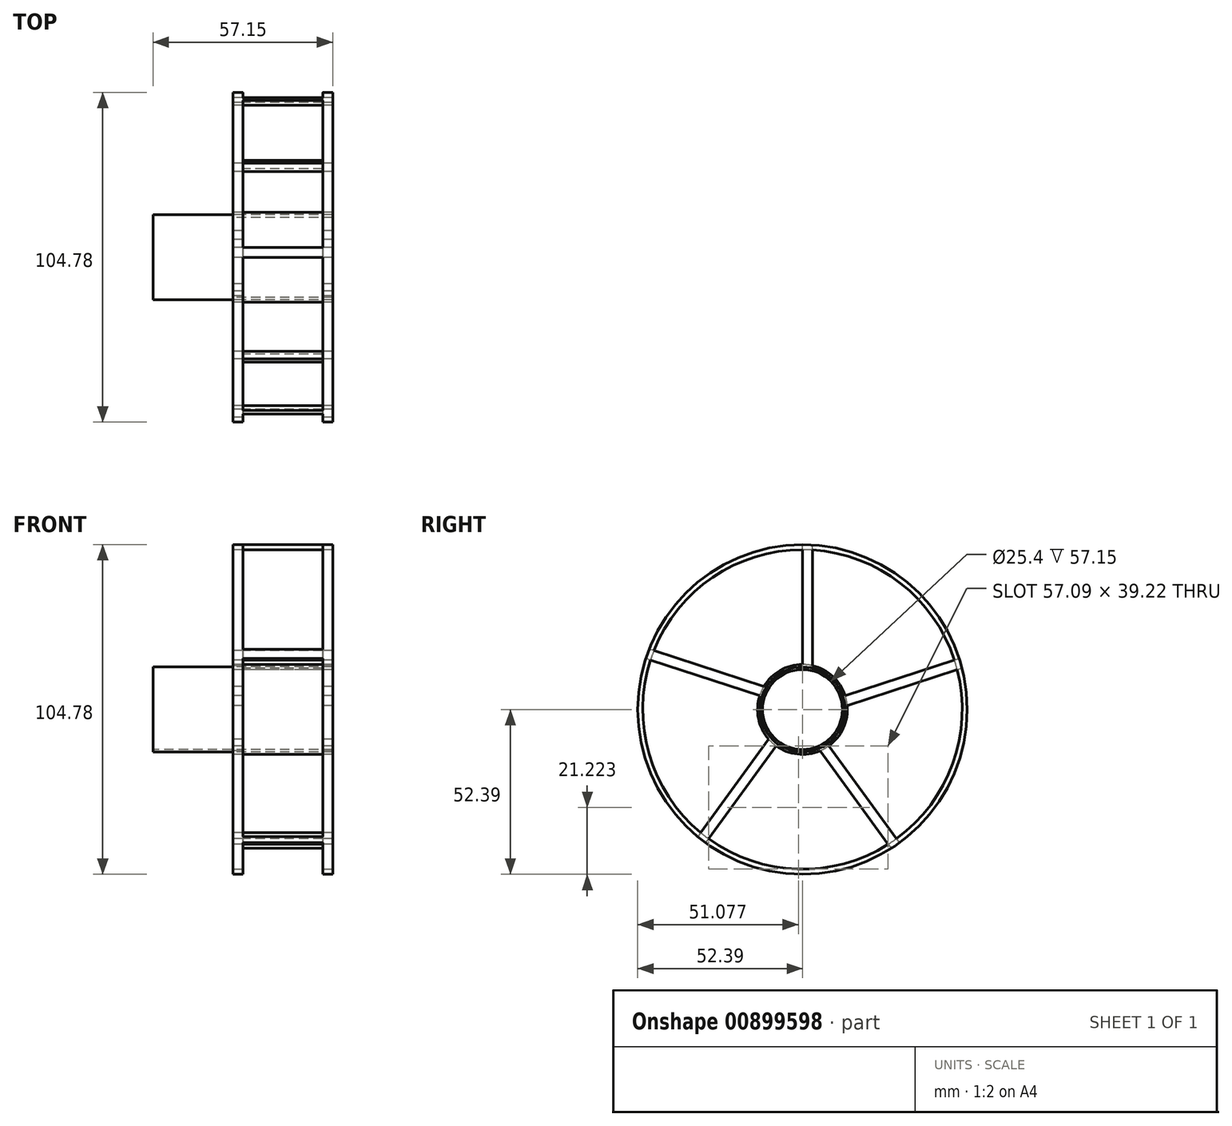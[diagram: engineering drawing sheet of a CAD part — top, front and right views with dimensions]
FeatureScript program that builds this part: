
annotation { "Feature Type Name" : "Feature", "Feature Type Description" : "" }
export const myFeature = defineFeature(function(context is Context, id is Id, definition is map)
    precondition{}
    {
        {
            var Q0;
            Q0=qCreatedBy(makeId("Right.planeOp"),FACE);
            var sketch = newSketch(context, id + "F0", { "sketchPlane" : qUnion([Q0])});
            skCircle(sketch, "E0", {"center": v(0, 0) * mm, "radius": 50.8 * mm});
            skCircle(sketch, "E1", {"center": v(0, 0) * mm, "radius": 52.39 * mm});
            skCircle(sketch, "E2", {"center": v(0, 0) * mm, "radius": 13.5 * mm});
            skCircle(sketch, "E3", {"center": v(0, 0) * mm, "radius": 12.7 * mm});
            skCircle(sketch, "E4", {"center": v(0, 0) * mm, "radius": 14.29 * mm});
            skLineSegment(sketch, "E5", {"start": v(0, 52.39) * mm, "end": v(0, 50.8) * mm});
            skLineSegment(sketch, "E6.0", {"start": v(3.17, 52.3) * mm, "end": v(3.17, 50.7) * mm});
            skLineSegment(sketch, "E7.1.0", {"start": v(-49.82, 16.19) * mm, "end": v(-48.31, 15.7) * mm});
            skLineSegment(sketch, "E7.1.1", {"start": v(-48.75, 19.18) * mm, "end": v(-47.24, 18.69) * mm});
            skLineSegment(sketch, "E7.2.0", {"start": v(-30.8, -42.38) * mm, "end": v(-29.86, -41.1) * mm});
            skLineSegment(sketch, "E7.2.1", {"start": v(-33.3, -40.44) * mm, "end": v(-32.37, -39.15) * mm});
            skLineSegment(sketch, "E7.3.0", {"start": v(30.8, -42.38) * mm, "end": v(29.86, -41.1) * mm});
            skLineSegment(sketch, "E7.3.1", {"start": v(28.17, -44.17) * mm, "end": v(27.23, -42.88) * mm});
            skLineSegment(sketch, "E7.4.0", {"start": v(49.82, 16.19) * mm, "end": v(48.31, 15.7) * mm});
            skLineSegment(sketch, "E7.4.1", {"start": v(50.71, 13.14) * mm, "end": v(49.2, 12.65) * mm});
            skLineSegment(sketch, "E8", {"start": v(0, 50.8) * mm, "end": v(0, 14.29) * mm});
            skLineSegment(sketch, "E9", {"start": v(3.17, 50.7) * mm, "end": v(3.17, 13.93) * mm});
            skLineSegment(sketch, "E10.1.0", {"start": v(-47.24, 18.69) * mm, "end": v(-12.27, 7.32) * mm});
            skLineSegment(sketch, "E10.1.1", {"start": v(-48.31, 15.7) * mm, "end": v(-13.59, 4.42) * mm});
            skLineSegment(sketch, "E10.2.0", {"start": v(-32.37, -39.15) * mm, "end": v(-10.76, -9.4) * mm});
            skLineSegment(sketch, "E10.2.1", {"start": v(-29.86, -41.1) * mm, "end": v(-8.4, -11.56) * mm});
            skLineSegment(sketch, "E10.3.0", {"start": v(27.23, -42.88) * mm, "end": v(5.62, -13.14) * mm});
            skLineSegment(sketch, "E10.3.1", {"start": v(29.86, -41.1) * mm, "end": v(8.4, -11.56) * mm});
            skLineSegment(sketch, "E10.4.0", {"start": v(49.2, 12.65) * mm, "end": v(14.23, 1.29) * mm});
            skLineSegment(sketch, "E10.4.1", {"start": v(48.31, 15.7) * mm, "end": v(13.59, 4.42) * mm});
            skSolve(sketch);
        }
        {
            var Q0;
            {var subQ0=sQuery(id+"F0.wireOp",EDGE,"E6.0");Q0=makeQuery(id+"F0.imprint","IMPRINT",FACE,{"disambiguationData":[TD([[makeQuery(id+"F0.imprint","IMPRINT",EDGE,{"derivedFrom":subQ0}),1.0]])]});}
            var Q1;
            {var subQ0=sQuery(id+"F0.wireOp",EDGE,"E7.2.0");Q1=makeQuery(id+"F0.imprint","IMPRINT",FACE,{"disambiguationData":[TD([[makeQuery(id+"F0.imprint","IMPRINT",EDGE,{"derivedFrom":subQ0}),-1.0]])]});}
            var Q2;
            {var subQ0=sQuery(id+"F0.wireOp",EDGE,"E5");Q2=makeQuery(id+"F0.imprint","IMPRINT",FACE,{"disambiguationData":[TD([[makeQuery(id+"F0.imprint","IMPRINT",EDGE,{"derivedFrom":subQ0}),1.0]])]});}
            var Q3;
            {var subQ0=sQuery(id+"F0.wireOp",EDGE,"E7.4.0");Q3=makeQuery(id+"F0.imprint","IMPRINT",FACE,{"disambiguationData":[TD([[makeQuery(id+"F0.imprint","IMPRINT",EDGE,{"derivedFrom":subQ0}),1.0]])]});}
            var Q4;
            {var subQ0=sQuery(id+"F0.wireOp",EDGE,"E7.3.0");Q4=makeQuery(id+"F0.imprint","IMPRINT",FACE,{"disambiguationData":[TD([[makeQuery(id+"F0.imprint","IMPRINT",EDGE,{"derivedFrom":subQ0}),-1.0]])]});}
            var Q5;
            {var subQ0=sQuery(id+"F0.wireOp",EDGE,"E5");Q5=makeQuery(id+"F0.imprint","IMPRINT",FACE,{"disambiguationData":[TD([[makeQuery(id+"F0.imprint","IMPRINT",EDGE,{"derivedFrom":subQ0}),-1.0]])]});}
            var Q6;
            {var subQ0=sQuery(id+"F0.wireOp",EDGE,"E7.1.0");Q6=makeQuery(id+"F0.imprint","IMPRINT",FACE,{"disambiguationData":[TD([[makeQuery(id+"F0.imprint","IMPRINT",EDGE,{"derivedFrom":subQ0}),-1.0]])]});}
            var Q7;
            {var subQ0=sQuery(id+"F0.wireOp",EDGE,"E7.1.0");Q7=makeQuery(id+"F0.imprint","IMPRINT",FACE,{"disambiguationData":[TD([[makeQuery(id+"F0.imprint","IMPRINT",EDGE,{"derivedFrom":subQ0}),1.0]])]});}
            var Q8;
            {var subQ0=sQuery(id+"F0.wireOp",EDGE,"E7.3.0");Q8=makeQuery(id+"F0.imprint","IMPRINT",FACE,{"disambiguationData":[TD([[makeQuery(id+"F0.imprint","IMPRINT",EDGE,{"derivedFrom":subQ0}),1.0]])]});}
            var Q9;
            {var subQ2=sQuery(id+"F0.wireOp",EDGE,"E10.2.0");Q9=makeQuery(id+"F0.imprint","IMPRINT",FACE,{"disambiguationData":[TD([[makeQuery(id+"F0.imprint","IMPRINT",EDGE,{"derivedFrom":subQ2}),-1.0]])]});}
            var Q10;
            {var subQ2=sQuery(id+"F0.wireOp",EDGE,"E10.4.0");Q10=makeQuery(id+"F0.imprint","IMPRINT",FACE,{"disambiguationData":[TD([[makeQuery(id+"F0.imprint","IMPRINT",EDGE,{"derivedFrom":subQ2}),-1.0]])]});}
            var Q11;
            {var subQ2=sQuery(id+"F0.wireOp",EDGE,"E10.3.0");Q11=makeQuery(id+"F0.imprint","IMPRINT",FACE,{"disambiguationData":[TD([[makeQuery(id+"F0.imprint","IMPRINT",EDGE,{"derivedFrom":subQ2}),-1.0]])]});}
            var Q12;
            {var subQ0=sQuery(id+"F0.wireOp",EDGE,"E8");Q12=makeQuery(id+"F0.imprint","IMPRINT",FACE,{"disambiguationData":[TD([[makeQuery(id+"F0.imprint","IMPRINT",EDGE,{"derivedFrom":subQ0}),1.0]])]});}
            var Q13;
            {var subQ0=sQuery(id+"F0.wireOp",EDGE,"E7.2.0");Q13=makeQuery(id+"F0.imprint","IMPRINT",FACE,{"disambiguationData":[TD([[makeQuery(id+"F0.imprint","IMPRINT",EDGE,{"derivedFrom":subQ0}),1.0]])]});}
            var Q14;
            Q14=makeQuery(id+"F0.imprint","IMPRINT",FACE,{"disambiguationData":[TD([[makeQuery(id+"F0.imprint","IMPRINT",EDGE,{"derivedFrom":sQuery(id+"F0.wireOp",EDGE,"E2")}),-1.0]])]});
            var Q15;
            {var subQ2=sQuery(id+"F0.wireOp",EDGE,"E10.1.0");Q15=makeQuery(id+"F0.imprint","IMPRINT",FACE,{"disambiguationData":[TD([[makeQuery(id+"F0.imprint","IMPRINT",EDGE,{"derivedFrom":subQ2}),-1.0]])]});}
            extrude(context, id + "F1", {"entities" : qUnion([Q0, Q1, Q2, Q3, Q4, Q5, Q6, Q7, Q8, Q9, Q10, Q11, Q12, Q13, Q14, Q15]), "depth" : 3.17 * mm, "offsetDistance" : 25.4 * mm});
        }
        {
            var Q0;
            {var subQ0=sQuery(id+"F0.wireOp",EDGE,"E7.4.0");Q0=makeQuery(id+"F0.imprint","IMPRINT",FACE,{"disambiguationData":[TD([[makeQuery(id+"F0.imprint","IMPRINT",EDGE,{"derivedFrom":subQ0}),1.0]])]});}
            var Q1;
            {var subQ0=sQuery(id+"F0.wireOp",EDGE,"E7.2.0");Q1=makeQuery(id+"F0.imprint","IMPRINT",FACE,{"disambiguationData":[TD([[makeQuery(id+"F0.imprint","IMPRINT",EDGE,{"derivedFrom":subQ0}),1.0]])]});}
            var Q2;
            {var subQ0=sQuery(id+"F0.wireOp",EDGE,"E5");Q2=makeQuery(id+"F0.imprint","IMPRINT",FACE,{"disambiguationData":[TD([[makeQuery(id+"F0.imprint","IMPRINT",EDGE,{"derivedFrom":subQ0}),1.0]])]});}
            var Q3;
            {var subQ0=sQuery(id+"F0.wireOp",EDGE,"E7.3.0");Q3=makeQuery(id+"F0.imprint","IMPRINT",FACE,{"disambiguationData":[TD([[makeQuery(id+"F0.imprint","IMPRINT",EDGE,{"derivedFrom":subQ0}),1.0]])]});}
            var Q4;
            {var subQ0=sQuery(id+"F0.wireOp",EDGE,"E7.1.0");Q4=makeQuery(id+"F0.imprint","IMPRINT",FACE,{"disambiguationData":[TD([[makeQuery(id+"F0.imprint","IMPRINT",EDGE,{"derivedFrom":subQ0}),1.0]])]});}
            var Q5;
            Q5=makeQuery(id+"F0.imprint","IMPRINT",FACE,{"disambiguationData":[TD([[makeQuery(id+"F0.imprint","IMPRINT",EDGE,{"derivedFrom":sQuery(id+"F0.wireOp",EDGE,"E2")}),-1.0]])]});
            extrude(context, id + "F2", {"entities" : qUnion([Q0, Q1, Q2, Q3, Q4, Q5]), "operationType" : NewBodyOperationType.ADD, "depth" : 28.57 * mm, "offsetDistance" : 25.4 * mm});
        }
        {
            var Q0;
            Q0=makeQuery(id+"F0.imprint","IMPRINT",FACE,{"disambiguationData":[TD([[makeQuery(id+"F0.imprint","IMPRINT",EDGE,{"derivedFrom":sQuery(id+"F0.wireOp",EDGE,"E2")}),-1.0]])]});
            var Q1;
            {var subQ2=sQuery(id+"F0.wireOp",EDGE,"E10.1.0");Q1=makeQuery(id+"F0.imprint","IMPRINT",FACE,{"disambiguationData":[TD([[makeQuery(id+"F0.imprint","IMPRINT",EDGE,{"derivedFrom":subQ2}),-1.0]])]});}
            var Q2;
            {var subQ0=sQuery(id+"F0.wireOp",EDGE,"E5");Q2=makeQuery(id+"F0.imprint","IMPRINT",FACE,{"disambiguationData":[TD([[makeQuery(id+"F0.imprint","IMPRINT",EDGE,{"derivedFrom":subQ0}),-1.0]])]});}
            var Q3;
            {var subQ0=sQuery(id+"F0.wireOp",EDGE,"E7.2.0");Q3=makeQuery(id+"F0.imprint","IMPRINT",FACE,{"disambiguationData":[TD([[makeQuery(id+"F0.imprint","IMPRINT",EDGE,{"derivedFrom":subQ0}),1.0]])]});}
            var Q4;
            {var subQ0=sQuery(id+"F0.wireOp",EDGE,"E7.1.0");Q4=makeQuery(id+"F0.imprint","IMPRINT",FACE,{"disambiguationData":[TD([[makeQuery(id+"F0.imprint","IMPRINT",EDGE,{"derivedFrom":subQ0}),1.0]])]});}
            var Q5;
            {var subQ0=sQuery(id+"F0.wireOp",EDGE,"E7.2.0");Q5=makeQuery(id+"F0.imprint","IMPRINT",FACE,{"disambiguationData":[TD([[makeQuery(id+"F0.imprint","IMPRINT",EDGE,{"derivedFrom":subQ0}),-1.0]])]});}
            var Q6;
            {var subQ2=sQuery(id+"F0.wireOp",EDGE,"E10.3.0");Q6=makeQuery(id+"F0.imprint","IMPRINT",FACE,{"disambiguationData":[TD([[makeQuery(id+"F0.imprint","IMPRINT",EDGE,{"derivedFrom":subQ2}),-1.0]])]});}
            var Q7;
            {var subQ0=sQuery(id+"F0.wireOp",EDGE,"E7.3.0");Q7=makeQuery(id+"F0.imprint","IMPRINT",FACE,{"disambiguationData":[TD([[makeQuery(id+"F0.imprint","IMPRINT",EDGE,{"derivedFrom":subQ0}),1.0]])]});}
            var Q8;
            {var subQ0=sQuery(id+"F0.wireOp",EDGE,"E6.0");Q8=makeQuery(id+"F0.imprint","IMPRINT",FACE,{"disambiguationData":[TD([[makeQuery(id+"F0.imprint","IMPRINT",EDGE,{"derivedFrom":subQ0}),1.0]])]});}
            var Q9;
            {var subQ0=sQuery(id+"F0.wireOp",EDGE,"E8");Q9=makeQuery(id+"F0.imprint","IMPRINT",FACE,{"disambiguationData":[TD([[makeQuery(id+"F0.imprint","IMPRINT",EDGE,{"derivedFrom":subQ0}),1.0]])]});}
            var Q10;
            {var subQ0=sQuery(id+"F0.wireOp",EDGE,"E5");Q10=makeQuery(id+"F0.imprint","IMPRINT",FACE,{"disambiguationData":[TD([[makeQuery(id+"F0.imprint","IMPRINT",EDGE,{"derivedFrom":subQ0}),1.0]])]});}
            var Q11;
            {var subQ2=sQuery(id+"F0.wireOp",EDGE,"E10.4.0");Q11=makeQuery(id+"F0.imprint","IMPRINT",FACE,{"disambiguationData":[TD([[makeQuery(id+"F0.imprint","IMPRINT",EDGE,{"derivedFrom":subQ2}),-1.0]])]});}
            var Q12;
            {var subQ0=sQuery(id+"F0.wireOp",EDGE,"E7.1.0");Q12=makeQuery(id+"F0.imprint","IMPRINT",FACE,{"disambiguationData":[TD([[makeQuery(id+"F0.imprint","IMPRINT",EDGE,{"derivedFrom":subQ0}),-1.0]])]});}
            var Q13;
            {var subQ2=sQuery(id+"F0.wireOp",EDGE,"E10.2.0");Q13=makeQuery(id+"F0.imprint","IMPRINT",FACE,{"disambiguationData":[TD([[makeQuery(id+"F0.imprint","IMPRINT",EDGE,{"derivedFrom":subQ2}),-1.0]])]});}
            var Q14;
            {var subQ0=sQuery(id+"F0.wireOp",EDGE,"E7.4.0");Q14=makeQuery(id+"F0.imprint","IMPRINT",FACE,{"disambiguationData":[TD([[makeQuery(id+"F0.imprint","IMPRINT",EDGE,{"derivedFrom":subQ0}),1.0]])]});}
            var Q15;
            {var subQ0=sQuery(id+"F0.wireOp",EDGE,"E7.3.0");Q15=makeQuery(id+"F0.imprint","IMPRINT",FACE,{"disambiguationData":[TD([[makeQuery(id+"F0.imprint","IMPRINT",EDGE,{"derivedFrom":subQ0}),-1.0]])]});}
            extrude(context, id + "F3", {"entities" : qUnion([Q0, Q1, Q2, Q3, Q4, Q5, Q6, Q7, Q8, Q9, Q10, Q11, Q12, Q13, Q14, Q15]), "operationType" : NewBodyOperationType.ADD, "depth" : 31.75 * mm, "offsetDistance" : 25.4 * mm, "hasSecondDirection" : true, "secondDirectionOppositeDirection" : false, "secondDirectionDepth" : 28.57 * mm});
        }
        {
            var Q0;
            Q0=makeQuery(id+"F0.imprint","IMPRINT",FACE,{"disambiguationData":[TD([[makeQuery(id+"F0.imprint","IMPRINT",EDGE,{"derivedFrom":sQuery(id+"F0.wireOp",EDGE,"E2")}),1.0]])]});
            extrude(context, id + "F4", {"entities" : qUnion([Q0]), "depth" : 31.75 * mm, "offsetDistance" : 25.4 * mm, "hasSecondDirection" : true, "secondDirectionOppositeDirection" : true, "secondDirectionDepth" : 25.4 * mm});
        }
        {
            var Q0;
            Q0=makeQuery(id+"F0.imprint","IMPRINT",FACE,{"disambiguationData":[TD([[makeQuery(id+"F0.imprint","IMPRINT",EDGE,{"derivedFrom":sQuery(id+"F0.wireOp",EDGE,"E2")}),1.0]])]});
            extrude(context, id + "F5", {"entities" : qUnion([Q0]), "depth" : 31.75 * mm, "offsetDistance" : 25.4 * mm});
        }
    });
